# Revit family: Flushometer-Toilet_Touchless-KOHLER-Tripoint-K-10957_1
name_source: partatom
category: Plumbing Fixtures
revit_build: Autodesk Revit 2017 (Build: 20160225_1515(x64)
units: mm (PartAtom-declared; Revit-internal decimal feet)

## family parameters
Cut with Voids When Loaded = No
Host = Face
OmniClass Number = 23.27.31.00
OmniClass Title = Valves
Part Type = Normal
Room Calculation Point = No
Round Connector Dimension = Use Diameter
Shared = No

## types (2) — shared parameters
ADA Compliant = Yes
Assembly Code = D2020
CW Connection = Yes
Cold Water Inlet = Cold Water Inlet
Cold Water Outlet = Cold Water Outlet
Date Modified = 02/04/2021
Default Elevation = 0"
Finish = Kohler-Metal-CP-Polished_Chrome
Flow Rate = 31 GPM
Flush Rate = 1.6 GPF
HW Connection = No
Hot Water Inlet = Hot Water Inlet
Manufacturer = KOHLER Co.
Master Format 2014 = 23 09 13.33
Master Format 2014 Name = Control Valves
Material = Brass Construction
Pressure = 80.00 psi
Product Documentation Link = https://www.us.kohler.com
Product Name = Tripoint
Product Page URL = http://www.us.kohler.com
RF Height = 8 1/16"
RF Length = 2 9/16"
RF Width = 3 1/4"
URL = https://www.us.kohler.com
Vent Connection = No
Waste Connection = No
Waste Water Outlet = Waste Water Outlet
WaterSense Certified = No

## per-type parameters (varying)
| type | Connector Dia 1 | Connector Dia 2 | Description | Model | Type | With_Accessories | Without_Accessories |
| 1.6 GPF Flushometer, CP-Polished Chrome | 0" | 1" | Touchless DC 1.6 gpf toilet flushometer | K-10957-CP | 1 | Yes | No |
| 1.6 GPF Retrofit Flushometer, CP-Polished Chrome | 1" | 0" | Touchless DC 1.6 gpf toilet flushometer retrofit | K-10957-RF-CP | 2 | No | Yes |

## geometry (parser evidence)
native form markers: Sweep x5
no freeform markers — native parametric forms only
